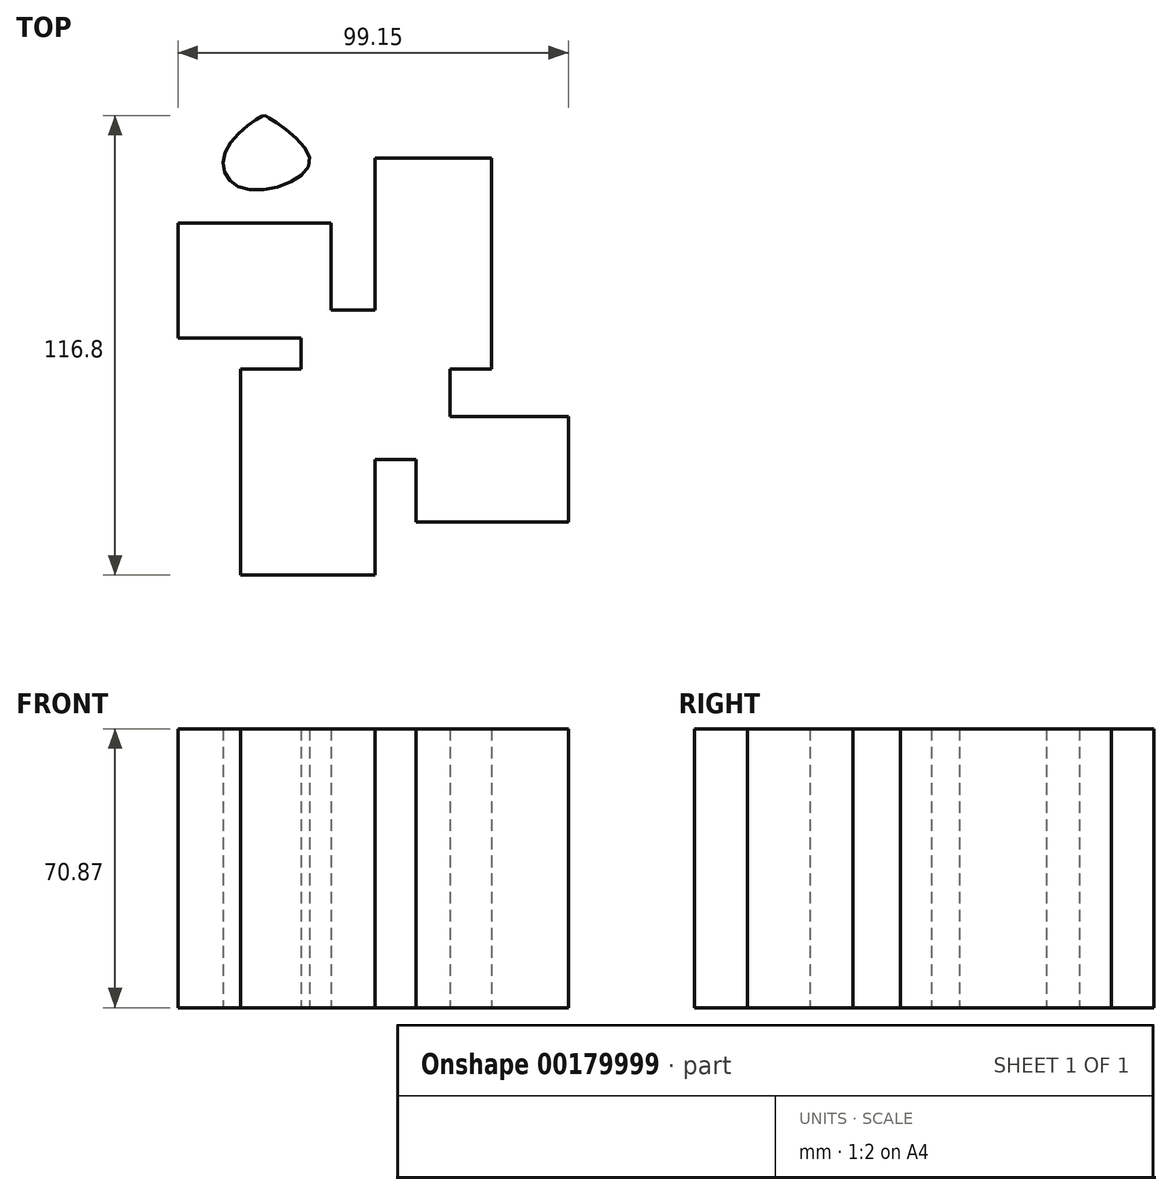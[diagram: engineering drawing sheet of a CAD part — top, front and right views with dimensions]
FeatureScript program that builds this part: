
annotation { "Feature Type Name" : "Feature", "Feature Type Description" : "" }
export const myFeature = defineFeature(function(context is Context, id is Id, definition is map)
    precondition{}
    {
        {
            var Q0;
            Q0=qCreatedBy(makeId("Top.planeOp"),FACE);
            var sketch = newSketch(context, id + "F0", { "sketchPlane" : qUnion([Q0])});
            skLineSegment(sketch, "E0.bottom", {"start": v(-18.74, 14.91) * mm, "end": v(19.15, 14.91) * mm});
            skLineSegment(sketch, "E0.top", {"start": v(-18.74, -22.98) * mm, "end": v(19.15, -22.98) * mm});
            skLineSegment(sketch, "E0.left", {"start": v(-18.74, 14.91) * mm, "end": v(-18.74, -22.98) * mm});
            skLineSegment(sketch, "E0.right", {"start": v(19.15, 14.91) * mm, "end": v(19.15, -22.98) * mm});
            skLineSegment(sketch, "E1.bottom", {"start": v(0, 0) * mm, "end": v(29.63, 0) * mm});
            skLineSegment(sketch, "E1.top", {"start": v(0, 53.6) * mm, "end": v(29.63, 53.6) * mm});
            skLineSegment(sketch, "E1.left", {"start": v(0, 0) * mm, "end": v(0, 53.6) * mm});
            skLineSegment(sketch, "E1.right", {"start": v(29.63, 0) * mm, "end": v(29.63, 53.6) * mm});
            skLineSegment(sketch, "E2.bottom", {"start": v(0, 0) * mm, "end": v(-34.06, 0) * mm});
            skLineSegment(sketch, "E2.top", {"start": v(0, -52.4) * mm, "end": v(-34.06, -52.4) * mm});
            skLineSegment(sketch, "E2.left", {"start": v(0, 0) * mm, "end": v(0, -52.4) * mm});
            skLineSegment(sketch, "E2.right", {"start": v(-34.06, 0) * mm, "end": v(-34.06, -52.4) * mm});
            skLineSegment(sketch, "E3.bottom", {"start": v(-11.08, 7.86) * mm, "end": v(-49.98, 7.86) * mm});
            skLineSegment(sketch, "E3.top", {"start": v(-11.08, 37.08) * mm, "end": v(-49.98, 37.08) * mm});
            skLineSegment(sketch, "E3.left", {"start": v(-11.08, 7.86) * mm, "end": v(-11.08, 37.08) * mm});
            skLineSegment(sketch, "E3.right", {"start": v(-49.98, 7.86) * mm, "end": v(-49.98, 37.08) * mm});
            skLineSegment(sketch, "E4.bottom", {"start": v(10.48, -12.1) * mm, "end": v(49.17, -12.1) * mm});
            skLineSegment(sketch, "E4.top", {"start": v(10.48, -38.9) * mm, "end": v(49.17, -38.9) * mm});
            skLineSegment(sketch, "E4.left", {"start": v(10.48, -12.1) * mm, "end": v(10.48, -38.9) * mm});
            skLineSegment(sketch, "E4.right", {"start": v(49.17, -12.1) * mm, "end": v(49.17, -38.9) * mm});
            skFitSpline(sketch, "E5", {"points": [v(-38.1, 55.02) * mm, v(-28.42, 64.3) * mm, v(-27, 63.89) * mm, v(-16.53, 52.8) * mm, v(-33.05, 45.75) * mm, v(-38.1, 55.02) * mm]});
            skSolve(sketch);
        }
        {
            var Q0;
            Q0 = qSketchRegion(id + "F0", true);
            extrude(context, id + "F1", {"entities" : qUnion([Q0]), "depth" : 70.87 * mm});
        }
    });
